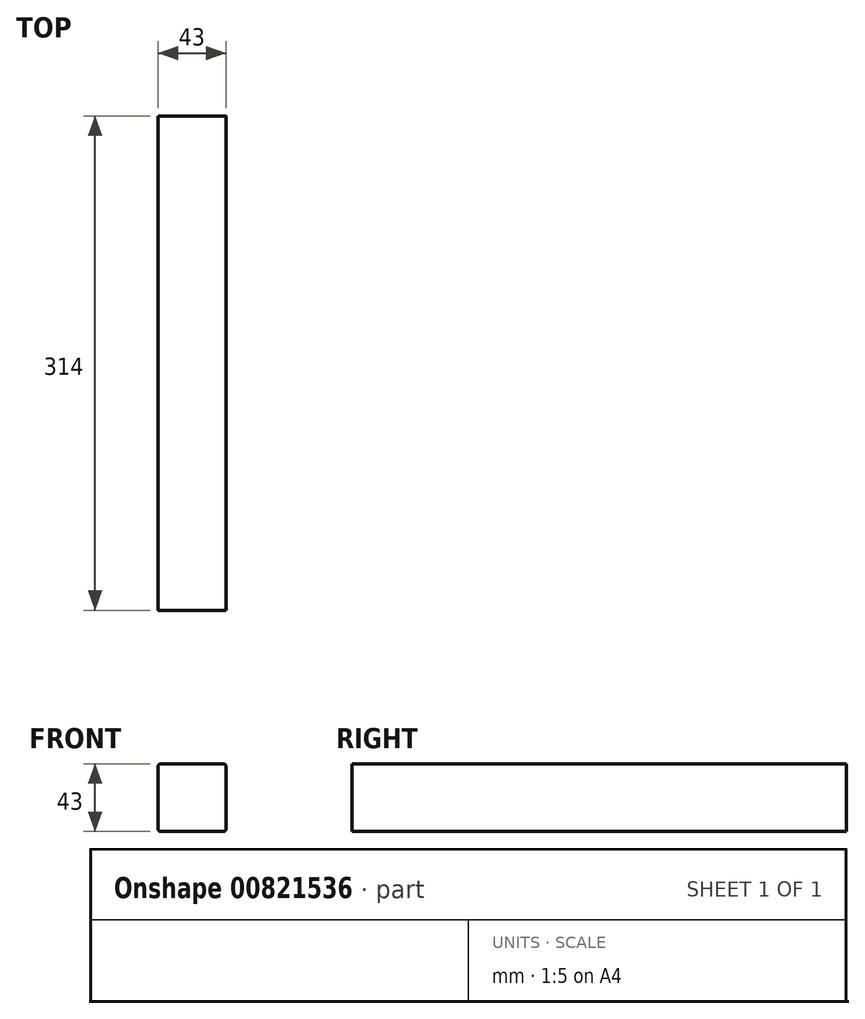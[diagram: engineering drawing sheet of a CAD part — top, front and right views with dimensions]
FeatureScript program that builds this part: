
annotation { "Feature Type Name" : "Feature", "Feature Type Description" : "" }
export const myFeature = defineFeature(function(context is Context, id is Id, definition is map)
    precondition{}
    {
        {
            var Q0;
            Q0=qCreatedBy(makeId("Front.planeOp"),FACE);
            var sketch = newSketch(context, id + "F0", { "sketchPlane" : qUnion([Q0])});
            skLineSegment(sketch, "E0.bottom", {"start": v(-21.5, 21.5) * mm, "end": v(21.5, 21.5) * mm});
            skLineSegment(sketch, "E0.top", {"start": v(-21.5, -21.5) * mm, "end": v(21.5, -21.5) * mm});
            skLineSegment(sketch, "E0.left", {"start": v(-21.5, 21.5) * mm, "end": v(-21.5, -21.5) * mm});
            skLineSegment(sketch, "E0.right", {"start": v(21.5, 21.5) * mm, "end": v(21.5, -21.5) * mm});
            skPoint(sketch, "E0.middle", {"position": v(0, 0) * mm});
            skSolve(sketch);
        }
        {
            var Q0;
            Q0=makeQuery(id+"F0.imprint","IMPRINT",FACE,{"disambiguationData":[TD([[makeQuery(id+"F0.imprint","IMPRINT",EDGE,{"derivedFrom":sQuery(id+"F0.wireOp",EDGE,"E0.bottom")}),-1.0]])]});
            extrude(context, id + "F1", {"entities" : qUnion([Q0]), "endBound" : BoundingType.SYMMETRIC, "depth" : 314 * mm, "offsetDistance" : 25 * mm});
        }
        {
            var Q0;
            Q0=makeQuery(id+"F1.opExtrude","SWEPT_EDGE",EDGE,{"disambiguationData":[OSD([sQuery(id+"F0.wireOp",EDGE,"E0.bottom"),sQuery(id+"F0.wireOp",EDGE,"E0.right")])]});
            var Q1;
            Q1=makeQuery(id+"F1.opExtrude","SWEPT_EDGE",EDGE,{"disambiguationData":[OSD([sQuery(id+"F0.wireOp",EDGE,"E0.bottom"),sQuery(id+"F0.wireOp",EDGE,"E0.left")])]});
            var Q2;
            Q2=makeQuery(id+"F1.opExtrude","SWEPT_EDGE",EDGE,{"disambiguationData":[OSD([sQuery(id+"F0.wireOp",EDGE,"E0.top"),sQuery(id+"F0.wireOp",EDGE,"E0.right")])]});
            var Q3;
            Q3=makeQuery(id+"F1.opExtrude","SWEPT_EDGE",EDGE,{"disambiguationData":[OSD([sQuery(id+"F0.wireOp",EDGE,"E0.top"),sQuery(id+"F0.wireOp",EDGE,"E0.left")])]});
            fillet(context, id + "F2", {"entities" : qUnion([Q0, Q1, Q2, Q3]), "radius" : 1.5 * mm, "tangentPropagation" : true, "allowEdgeOverflow" : false});
        }
    });
